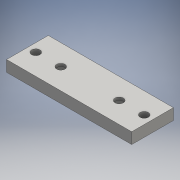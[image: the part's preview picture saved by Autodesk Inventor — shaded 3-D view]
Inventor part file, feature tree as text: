
AUTODESK INVENTOR PART (.ipt)
format: ipt  version: 2016 SP1 (Build 200210100, 210)  size: 128,000 bytes
history: native  units: mm
features: extrude x4, sketch x4, projected_geometry x2
ambient origin geometry x8: Origin, YZ Plane, XZ Plane, XY Plane, X Axis, Y Axis, Z Axis, Center Point
bodies: Solid1 (feature_tree)
feature tree (10):
  extrude  "Extrusion1"  Depth=16.0mm
  extrude  "Extrusion2"  Depth=21.0mm
  extrude  "Extrusion3"  Depth=30.0mm
  extrude  "Extrusion4"  Depth=2.0mm
  sketch  "Sketch1"  dims[d0=16.0mm d1=16.0mm]
  sketch  "Sketch2"  dims[d2=42.0mm d3=21.0mm]
  sketch  "Sketch3"  dims[d4=15.0mm d5=30.0mm]
  projected_geometry  "Projected Loop1"
  projected_geometry  "Projected Loop2"
  sketch  "Sketch4"  dims[d6=16.0mm d7=16.0mm d8=8.0mm d9=0.0mm d10=2.0mm d11=0.0mm d12=6.0mm d13=6.0mm d14=2.0mm d15=0.0mm d16=6.0mm d17=6.0mm d18=6.0mm d19=6.0mm d20=2.0mm d21=0.0mm]
